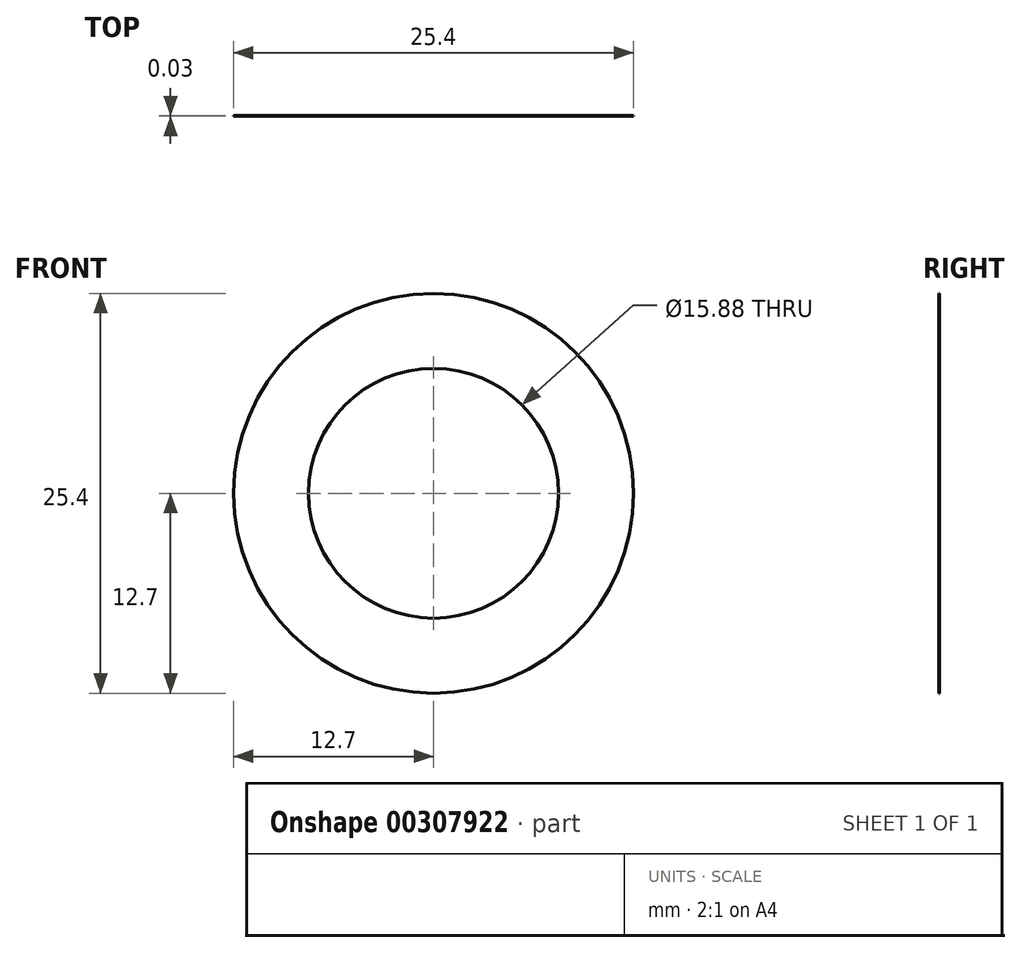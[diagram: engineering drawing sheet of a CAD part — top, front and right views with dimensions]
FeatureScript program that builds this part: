
annotation { "Feature Type Name" : "Feature", "Feature Type Description" : "" }
export const myFeature = defineFeature(function(context is Context, id is Id, definition is map)
    precondition{}
    {
        {
            var Q0;
            Q0=qCreatedBy(makeId("Front.planeOp"),FACE);
            var sketch = newSketch(context, id + "F0", { "sketchPlane" : qUnion([Q0])});
            skCircle(sketch, "E0", {"center": v(0, 0) * mm, "radius": 12.7 * mm});
            skSolve(sketch);
        }
        {
            var Q0;
            Q0 = qSketchRegion(id + "F0", true);
            extrude(context, id + "F1", {"entities" : qUnion([Q0]), "depth" : 13 / 406.4 * mm});
        }
        {
            var Q0;
            Q0=qCreatedBy(makeId("Front.planeOp"),FACE);
            var sketch = newSketch(context, id + "F2", { "sketchPlane" : qUnion([Q0])});
            skCircle(sketch, "E1", {"center": v(0, 0) * mm, "radius": 7.94 * mm});
            skSolve(sketch);
        }
        {
            var Q0;
            Q0 = qSketchRegion(id + "F2", true);
            extrude(context, id + "F3", {"entities" : qUnion([Q0]), "operationType" : NewBodyOperationType.REMOVE, "depth" : 13 / 406.4 * mm});
        }
    });
